# Revit family: Stoßstellenleiste
name_source: partatom
category: Generic Models
revit_build: Autodesk Revit 2015 (Build: 20140606_1530(x64)
units: mm (PartAtom-declared; Revit-internal decimal feet)

## types (14) — shared parameters
Manufacturer = OBO Bettermann
Material = Steel, Galvanized
URL = http://www.obo-bettermann.com

## per-type parameters (varying)
| type | GTIN | Manufacturer Art.No. | Width |
| SSLB 100 FS | 4012196079971 | 7070205 | 85 mm  [stored 0.278871 ft] |
| SSLB 150 FS | 4012196094820 | 7070209 | 135 mm  [stored 0.442913 ft] |
| SSLB 200 FS | 4012196094882 | 7070213 | 185 mm  [stored 0.606955 ft] |
| SSLB 300 FS | 4012196094943 | 7070217 | 285 mm  [stored 0.935039 ft] |
| SSLB 400 FS | 4012196095001 | 7070221 | 385 mm  [stored 1.26312 ft] |
| SSLB 500 FS | 4012196095063 | 7070225 | 485 mm  [stored 1.59121 ft] |
| SSLB 600 FS | 4012196095186 | 7070233 | 585 mm  [stored 1.91929 ft] |
| SSLB 100 DD | 4012196095186 | 7070306 | 85 mm  [stored 0.278871 ft] |
| SSLB 150 DD | 4012196095308 | 7070310 | 135 mm  [stored 0.442913 ft] |
| SSLB 200 DD | 4012196095360 | 7070314 | 185 mm  [stored 0.606955 ft] |
| SSLB 300 DD | 4012196095421 | 7070318 | 285 mm  [stored 0.935039 ft] |
| SSLB 400 DD | 4012196095483 | 7070322 | 385 mm  [stored 1.26312 ft] |
| SSLB 500 DD | 4012196095544 | 7070326 | 485 mm  [stored 1.59121 ft] |
| SSLB 600 DD | 4012196095667 | 7070334 | 485 mm  [stored 1.59121 ft] |

note: column(s) folded — value = type name in every type: Article Type

note: [stored X ft] marks values corroborated as IEEE doubles in the binary element streams (Revit-internal decimal feet)

## geometry (parser evidence)
native form markers: Sweep x5
no freeform markers — native parametric forms only
